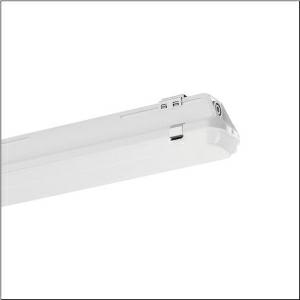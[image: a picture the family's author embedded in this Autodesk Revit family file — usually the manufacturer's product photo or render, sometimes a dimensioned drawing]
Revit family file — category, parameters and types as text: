
# Revit family: monsun_r__21_51fb20fp430c_ff39
name_source: partatom
category: Lighting Fixtures
units: mm (PartAtom-declared; Revit-internal decimal feet)

## family parameters
Cut with Voids When Loaded = No
Host = Face
Light Source = No
Part Type = Normal
Room Calculation Point = No
Round Connector Dimension = Use Diameter
Shared = No

## types (1)
- --- (1 x LED, 3000 lm, 18.9 W, 4000K)
    Apparent Load = 19 VA
    CIE Flux Codes = 45 75 93 94 100
    Color Rendering = 80
    Color Temperature = 4000K
    Default Elevation = 1800 mm
    Description = Monsun® 21, damp-proof luminaire, chain hanger, primary optical cover: enclosure, of PC, light emission: direct distribution, primary light characteristic: symmetric, installation type: suspended mounting, surface-mounted, horizontal mounting, vertical mounting, LED, rated luminous flux: 3.000lm, luminous efficacy: 159lm/W, light colour: 840, colour temperature: 4000K, control gear: DALI, CLO, with terminal, 3-pole, max. 2.5mm², mains connection: 220..240V, AC, 50/60Hz, rated input power: 19W, housing, of PC, uncoated, bright grey, incl. chain hanger, length: 1.590mm, width: 90mm, height: 88mm, clip for enclosure, of stainless steel (V2A), ceiling mounting element, of stainless steel (V2A), chain hanger, of stainless steel (V2A), protection rating (complete): IP66, insulation class (complete): insulation class I (protective earthing), certification: CE, ENEC, VDE, UKCA, protection symbol: D, impact resistance: IK08, permissible operating ambient temperature: -25..+35°C, standard: EN 50419, EN 60598-2-1, corresponds to IFS (International Featured Standards) requirements for safety and quality in the food industry, for indoor or canopied outdoor use, no direct snow, no direct sun, no direct rain, LABS conformity tested according to VDMA 24364:2018-05, contact your sales advisor before using the luminaires in applications with unclear chemical exposure, large temperature fluctuations or condensation-forming humidity, packaging unit: 1 piece
    Height = 89 mm
    Lamp = 1 x LED
    Lamp Light Flux = 3000 lm
    Lamp Power = 18.9 W
    Lamp count = 1
    Length = 1590 mm
    Luminous efficacy = 159 lm/W
    Manufacturer = Siteco
    ModVariant = No
    Model = 51FB20FP430C
    Mounting Place = Ceiling
    Mounting Type = Surface mounted
    Number of Poles = 1
    OnlyDefault = Yes
    Power Factor = 1
    Product Name = Monsun® 21
    Product group = damp-proof luminaire
    ProductGroupID = 301
    Protection Class = Protection class I
    Protection Degree = IP 66
    RLX_Detail_Level = 1
    RLX_Emergency_Light_Flux = 0 lm
    RLX_Emergency_Type = 0
    RLX_Emergency_Type_DB = No
    RlxData = <blob elided: 92041 chars, md5=fcf22696>
    Socket = socket
    Standby Power = 0 W
    System Light Flux = 3000 lm
    System Power = 19 W
    Type Comments = factory setting: luminous flux: 100 % | dim-lin: 254 | 124 mA
    Type Image = l_1319656.jpg
    URL = http://relux.com
    VarID = @adj_062627
    Voltage = 0 V
    Weight = 0.00 kg
    Width = 90 mm

## geometry (parser evidence)
native form markers: Blend x4, Sweep x15
no freeform markers — native parametric forms only
